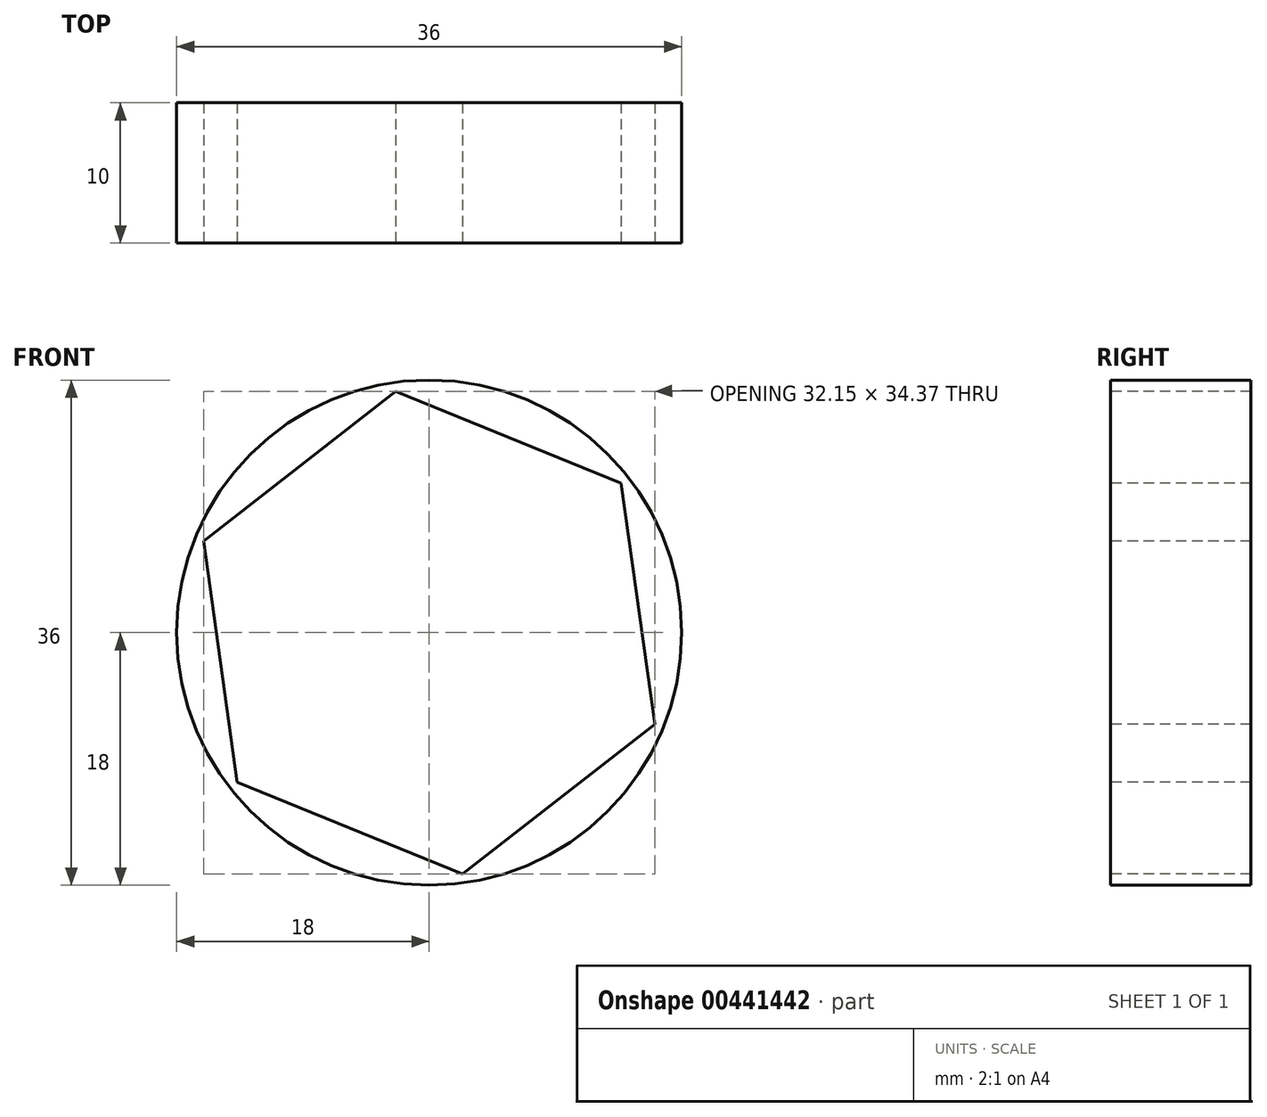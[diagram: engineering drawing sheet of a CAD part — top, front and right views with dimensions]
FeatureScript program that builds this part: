
annotation { "Feature Type Name" : "Feature", "Feature Type Description" : "" }
export const myFeature = defineFeature(function(context is Context, id is Id, definition is map)
    precondition{}
    {
        {
            var Q0;
            Q0=qCreatedBy(makeId("Front.planeOp"),FACE);
            var sketch = newSketch(context, id + "F0", { "sketchPlane" : qUnion([Q0])});
            skCircle(sketch, "E0", {"center": v(0, 0) * mm, "radius": 18 * mm});
            skCircle(sketch, "E1.cCircle", {"center": v(0, 0) * mm, "radius": 15.03 * mm, "construction": true});
            skLineSegment(sketch, "E1.0", {"start": v(-2.39, 17.18) * mm, "end": v(13.69, 10.66) * mm});
            skLineSegment(sketch, "E1.1", {"start": v(13.69, 10.66) * mm, "end": v(16.08, -6.53) * mm});
            skLineSegment(sketch, "E1.2", {"start": v(16.08, -6.53) * mm, "end": v(2.39, -17.18) * mm});
            skLineSegment(sketch, "E1.3", {"start": v(2.39, -17.18) * mm, "end": v(-13.69, -10.66) * mm});
            skLineSegment(sketch, "E1.4", {"start": v(-13.69, -10.66) * mm, "end": v(-16.08, 6.53) * mm});
            skLineSegment(sketch, "E1.5", {"start": v(-16.08, 6.53) * mm, "end": v(-2.39, 17.18) * mm});
            skPoint(sketch, "E1.0.midPoint", {"position": v(5.65, 13.92) * mm});
            skSolve(sketch);
        }
        {
            var Q0;
            Q0 = qSketchRegion(id + "F0", true);
            extrude(context, id + "F1", {"entities" : qUnion([Q0]), "oppositeDirection" : true, "depth" : 10 * mm});
        }
    });
